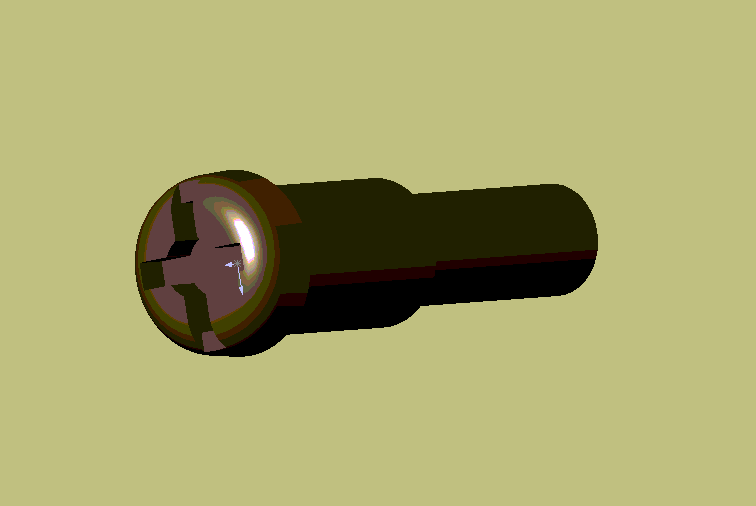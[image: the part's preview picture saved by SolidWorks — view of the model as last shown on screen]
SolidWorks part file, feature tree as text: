
SOLIDWORKS PART (.sldprt)
format: sldprt  version: not decoded by parser v0  size: 164,864 bytes
history: native  units: mm
features: sketch x5, plane x3, extrude x3, cut_extrude x2, material x1, fillet x1, chamfer x1 (+8 scaffold rows collapsed)
feature tree (24):
  scaffold x8  (default folders/planes/origin — collapsed)
  material  "Matériau <non spécifié>"
  plane  "Plane1"
  plane  "Plane2"
  plane  "Plane3"
  sketch  "Esquisse1"  dims[D1=5.0mm]
  extrude  "Base-Extrusion"  Depth=2mm
  fillet  "Congé1"  Radius=1mm
  sketch  "Esquisse2"  dims[D1=4.0mm]
  extrude  "Boss.-Extru.1"  Depth=6mm
  sketch  "Esquisse3"  dims[D1=3.0mm]
  extrude  "Boss.-Extru.2"  Depth=8mm
  chamfer  "Chanfrein1"  Distance=0.5mm Angle=45deg
  sketch  "Esquisse4"  dims[D1=0.75mm D2=1.0mm D3=0.75mm]
  cut_extrude  "Enlèv. mat.-Extru.1"  Depth=1mm
  sketch  "Esquisse5"
  cut_extrude  "Enlèv. mat.-Extru.2"  Depth=0.5mm
decode coverage: 11 of 12 modeling features carry decoded parameters
note: suppression state not decoded; provenance and decode notes live in map.json
